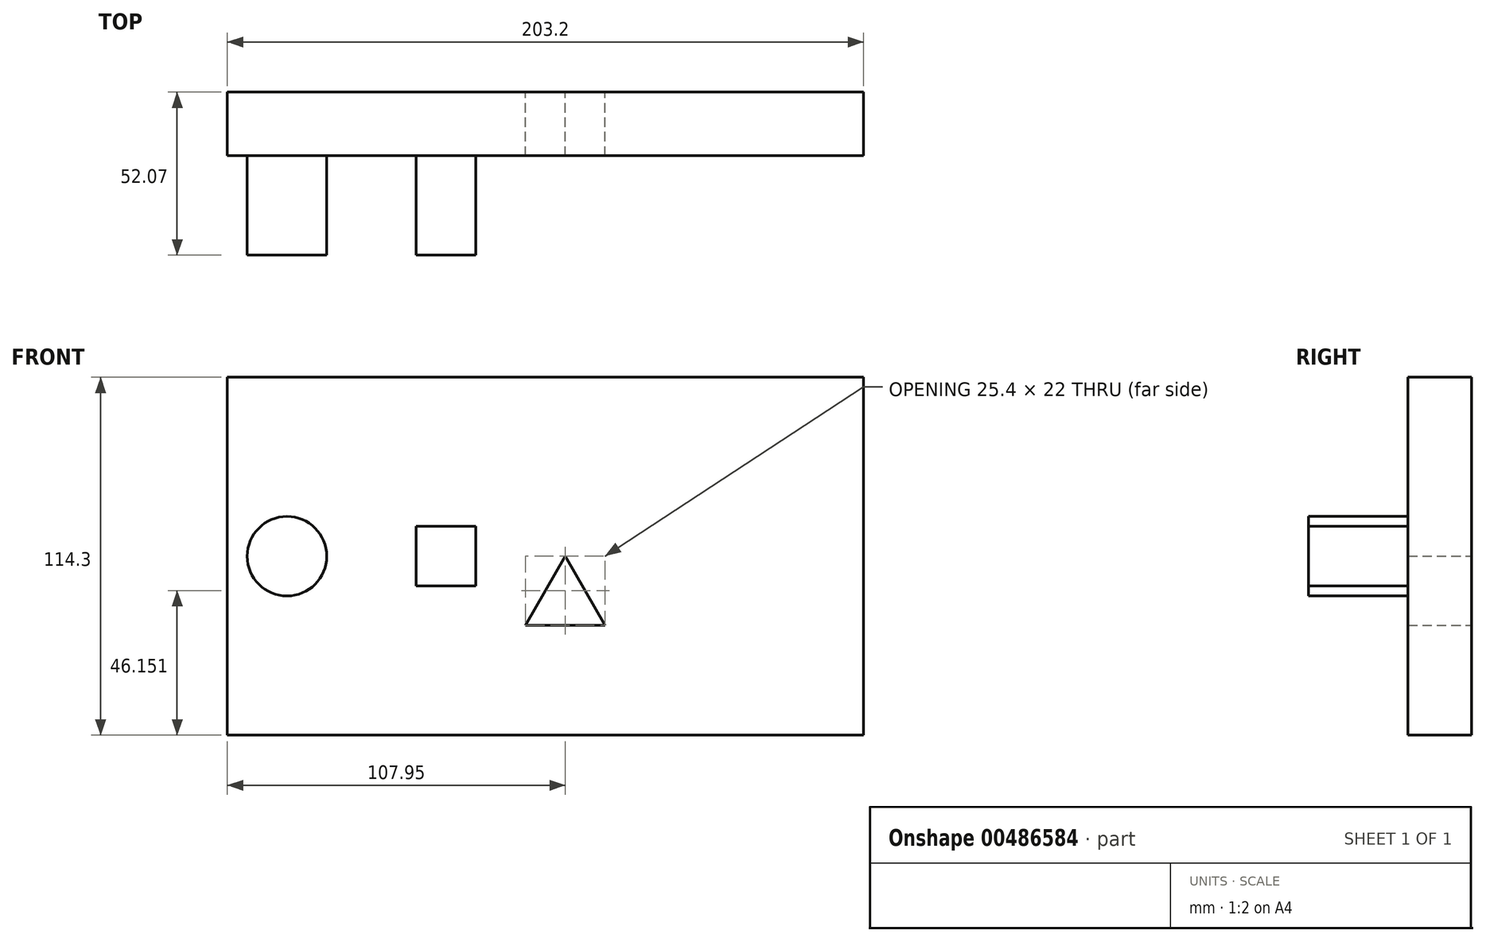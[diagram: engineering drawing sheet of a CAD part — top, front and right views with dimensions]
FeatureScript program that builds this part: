
annotation { "Feature Type Name" : "Feature", "Feature Type Description" : "" }
export const myFeature = defineFeature(function(context is Context, id is Id, definition is map)
    precondition{}
    {
        {
            var Q0;
            Q0=qCreatedBy(makeId("Front.planeOp"),FACE);
            var sketch = newSketch(context, id + "F0", { "sketchPlane" : qUnion([Q0])});
            skLineSegment(sketch, "E0.bottom", {"start": v(101.6, 57.15) * mm, "end": v(-101.6, 57.15) * mm});
            skLineSegment(sketch, "E0.top", {"start": v(101.6, -57.15) * mm, "end": v(-101.6, -57.15) * mm});
            skLineSegment(sketch, "E0.left", {"start": v(101.6, 57.15) * mm, "end": v(101.6, -57.15) * mm});
            skLineSegment(sketch, "E0.right", {"start": v(-101.6, 57.15) * mm, "end": v(-101.6, -57.15) * mm});
            skPoint(sketch, "E0.middle", {"position": v(0, 0) * mm});
            skLineSegment(sketch, "E1", {"start": v(0, 0) * mm, "end": v(6.35, 0) * mm});
            skLineSegment(sketch, "E2", {"start": v(0, 0) * mm, "end": v(-31.75, 0) * mm});
            skLineSegment(sketch, "E3", {"start": v(-31.75, 0) * mm, "end": v(-82.55, 0) * mm});
            skPoint(sketch, "E3.endSnap0", {"position": v(-101.6, 0) * mm});
            skLineSegment(sketch, "E4.bottom", {"start": v(-22.22, 9.53) * mm, "end": v(-41.27, 9.53) * mm});
            skLineSegment(sketch, "E4.top", {"start": v(-22.22, -9.53) * mm, "end": v(-41.27, -9.53) * mm});
            skLineSegment(sketch, "E4.left", {"start": v(-22.22, 9.53) * mm, "end": v(-22.23, -9.53) * mm});
            skLineSegment(sketch, "E4.right", {"start": v(-41.27, 9.53) * mm, "end": v(-41.27, -9.53) * mm});
            skPoint(sketch, "E4.middle", {"position": v(-31.75, 0) * mm});
            skCircle(sketch, "E5", {"center": v(-82.55, 0) * mm, "radius": 12.7 * mm});
            skLineSegment(sketch, "E6", {"start": v(6.35, 0) * mm, "end": v(-6.35, -22) * mm});
            skLineSegment(sketch, "E7", {"start": v(-6.35, -22) * mm, "end": v(19.05, -22) * mm});
            skLineSegment(sketch, "E8", {"start": v(19.05, -22) * mm, "end": v(6.35, 0) * mm});
            skSolve(sketch);
        }
        {
            var Q0;
            Q0=makeQuery(id+"F0.imprint","IMPRINT",FACE,{"disambiguationData":[TD([[makeQuery(id+"F0.imprint","IMPRINT",EDGE,{"derivedFrom":sQuery(id+"F0.wireOp",EDGE,"E0.bottom")}),1.0]])]});
            extrude(context, id + "F1", {"entities" : qUnion([Q0]), "depth" : 20.32 * mm});
        }
        {
            var Q0;
            Q0=makeQuery(id+"F0.imprint","IMPRINT",FACE,{"disambiguationData":[TD([[makeQuery(id+"F0.imprint","IMPRINT",EDGE,{"derivedFrom":sQuery(id+"F0.wireOp",EDGE,"E5")}),1.0]])]});
            var Q1;
            {var subQ1=sQuery(id+"F0.wireOp",EDGE,"E4.bottom");Q1=makeQuery(id+"F0.imprint","IMPRINT",FACE,{"disambiguationData":[TD([[makeQuery(id+"F0.imprint","IMPRINT",EDGE,{"derivedFrom":subQ1}),1.0]])]});}
            var Q2;
            {var subQ0=sQuery(id+"F0.wireOp",EDGE,"E4.top");Q2=makeQuery(id+"F0.imprint","IMPRINT",FACE,{"disambiguationData":[TD([[makeQuery(id+"F0.imprint","IMPRINT",EDGE,{"derivedFrom":subQ0}),-1.0]])]});}
            extrude(context, id + "F2", {"entities" : qUnion([Q0, Q1, Q2]), "operationType" : NewBodyOperationType.ADD, "depth" : 52.07 * mm});
        }
    });
